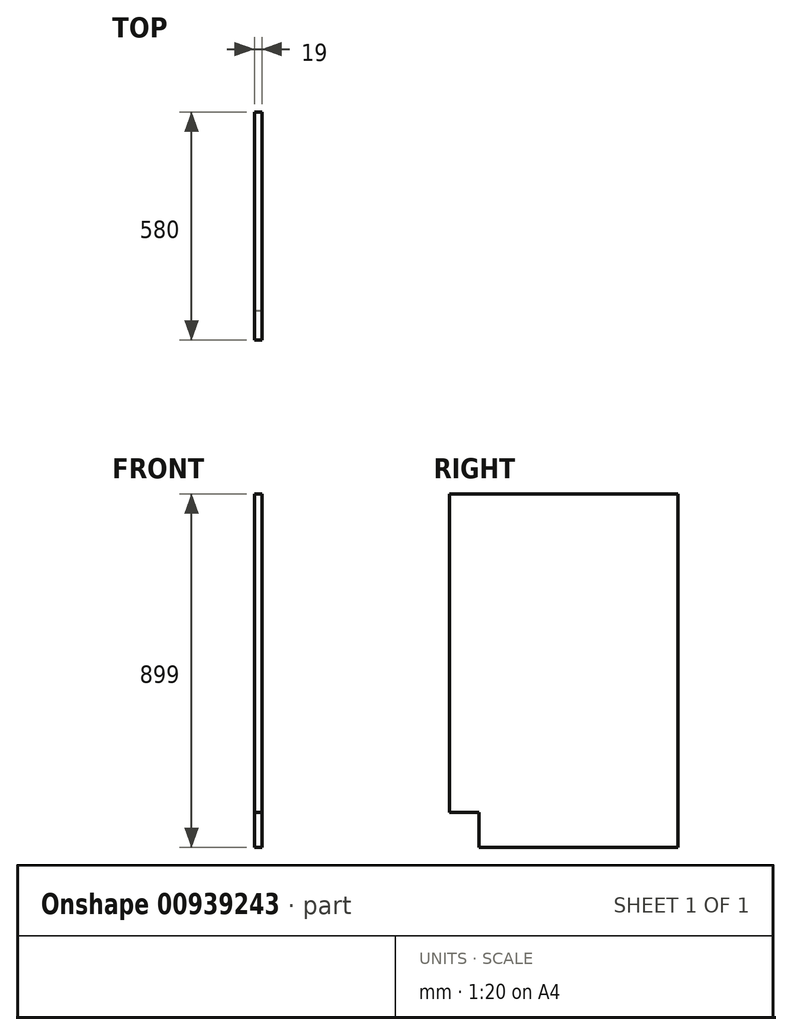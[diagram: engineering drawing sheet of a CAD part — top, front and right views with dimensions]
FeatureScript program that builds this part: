
annotation { "Feature Type Name" : "Feature", "Feature Type Description" : "" }
export const myFeature = defineFeature(function(context is Context, id is Id, definition is map)
    precondition{}
    {
        {
            var Q0;
            Q0=qCreatedBy(makeId("Right.planeOp"),FACE);
            var sketch = newSketch(context, id + "F0", { "sketchPlane" : qUnion([Q0])});
            skLineSegment(sketch, "E0.bottom", {"start": v(0, 0) * mm, "end": v(-505, 0) * mm});
            skLineSegment(sketch, "E0.top", {"start": v(0, 899) * mm, "end": v(-580, 899) * mm});
            skLineSegment(sketch, "E0.left", {"start": v(0, 0) * mm, "end": v(0, 899) * mm});
            skLineSegment(sketch, "E0.right", {"start": v(-580, 90) * mm, "end": v(-580, 899) * mm});
            skLineSegment(sketch, "E1", {"start": v(-505, 0) * mm, "end": v(-505, 90) * mm});
            skLineSegment(sketch, "E2", {"start": v(-505, 90) * mm, "end": v(-580, 90) * mm});
            skSolve(sketch);
        }
        {
            var Q0;
            Q0 = qSketchRegion(id + "F0", true);
            extrude(context, id + "F1", {"entities" : qUnion([Q0]), "oppositeDirection" : true, "depth" : 19 * mm, "offsetDistance" : 25 * mm});
        }
    });
